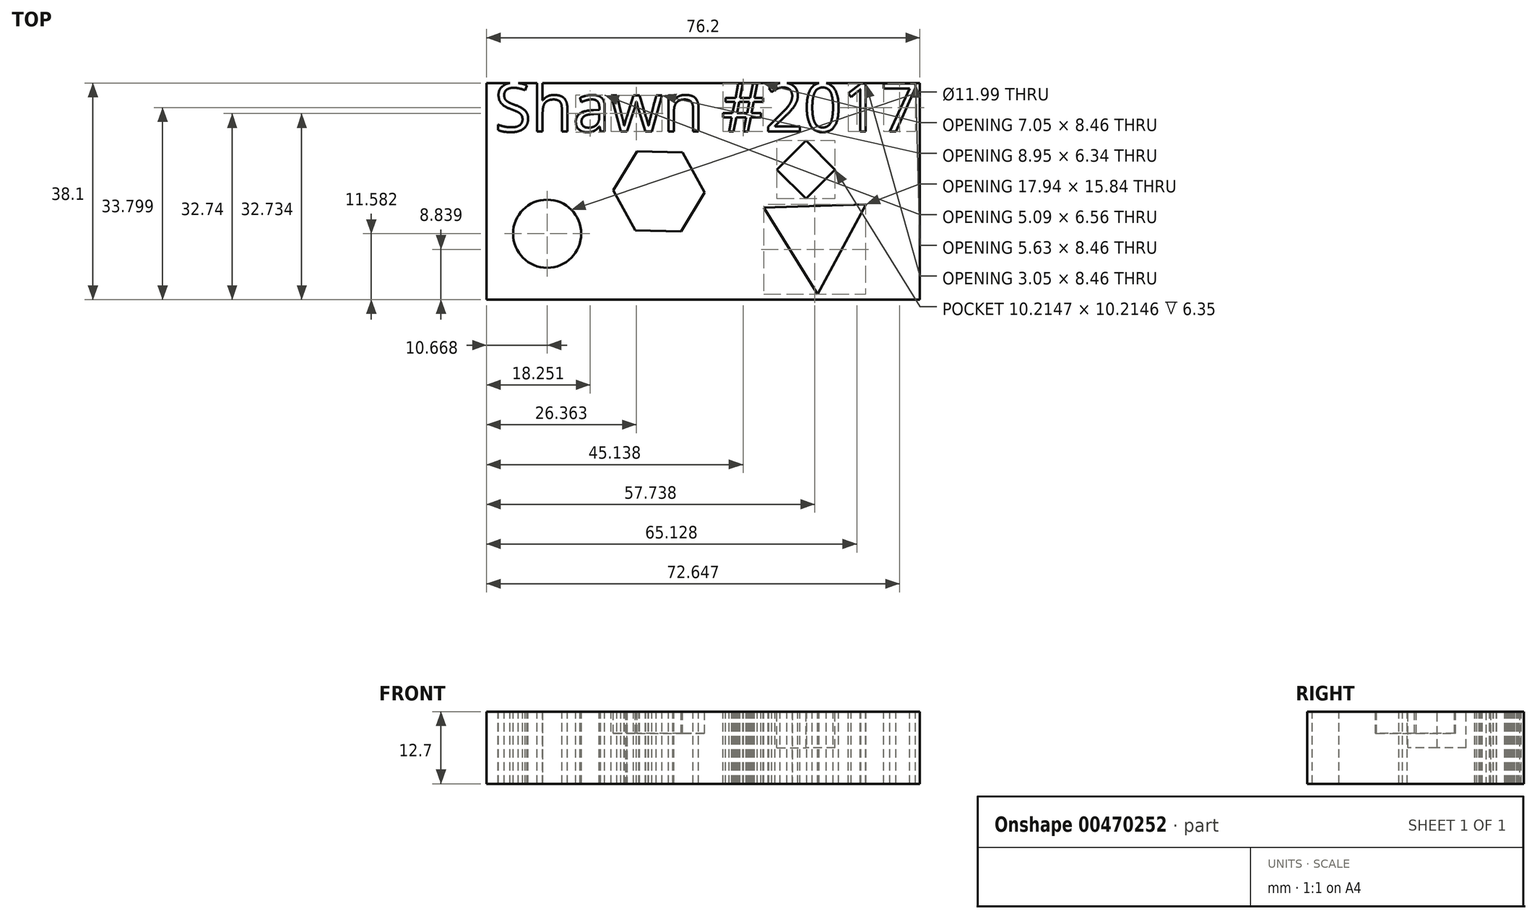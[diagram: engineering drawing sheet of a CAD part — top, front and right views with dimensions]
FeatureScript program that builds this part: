
annotation { "Feature Type Name" : "Feature", "Feature Type Description" : "" }
export const myFeature = defineFeature(function(context is Context, id is Id, definition is map)
    precondition{}
    {
        {
            var Q0;
            Q0=qCreatedBy(makeId("Top.planeOp"),FACE);
            var sketch = newSketch(context, id + "F0", { "sketchPlane" : qUnion([Q0])});
            skLineSegment(sketch, "E0.bottom", {"start": v(38.1, -19.05) * mm, "end": v(-38.1, -19.05) * mm});
            skLineSegment(sketch, "E0.top", {"start": v(38.1, 19.05) * mm, "end": v(-38.1, 19.05) * mm});
            skLineSegment(sketch, "E0.left", {"start": v(38.1, -19.05) * mm, "end": v(38.1, 19.05) * mm});
            skLineSegment(sketch, "E0.right", {"start": v(-38.1, -19.05) * mm, "end": v(-38.1, 19.05) * mm});
            skPoint(sketch, "E0.middle", {"position": v(0, 0) * mm});
            skSolve(sketch);
        }
        {
            var Q0;
            Q0 = qSketchRegion(id + "F0", true);
            extrude(context, id + "F1", {"entities" : qUnion([Q0]), "depth" : 12.7 * mm});
        }
        {
            var Q0;
            Q0=makeQuery(id+"F1.opExtrude","CAP_FACE",FACE,{"disambiguationData":[OSD([sQuery(id+"F0.wireOp",EDGE,"E0.bottom"),sQuery(id+"F0.wireOp",EDGE,"E0.top"),sQuery(id+"F0.wireOp",EDGE,"E0.left"),sQuery(id+"F0.wireOp",EDGE,"E0.right")])],"isStart":false});
            var sketch = newSketch(context, id + "F2", { "sketchPlane" : qUnion([Q0])});
            skCircle(sketch, "E1.cCircle", {"center": v(-7.77, 0) * mm, "radius": 6.96 * mm, "construction": true});
            skLineSegment(sketch, "E1.0", {"start": v(-11.93, -6.87) * mm, "end": v(-15.8, 0.17) * mm});
            skLineSegment(sketch, "E1.1", {"start": v(-15.8, 0.17) * mm, "end": v(-11.64, 7.04) * mm});
            skLineSegment(sketch, "E1.2", {"start": v(-11.64, 7.04) * mm, "end": v(-3.61, 6.87) * mm});
            skLineSegment(sketch, "E1.3", {"start": v(-3.61, 6.87) * mm, "end": v(0.26, -0.17) * mm});
            skLineSegment(sketch, "E1.4", {"start": v(0.26, -0.17) * mm, "end": v(-3.9, -7.04) * mm});
            skLineSegment(sketch, "E1.5", {"start": v(-3.9, -7.04) * mm, "end": v(-11.93, -6.87) * mm});
            skPoint(sketch, "E1.0.midPoint", {"position": v(-13.87, -3.35) * mm});
            skSolve(sketch);
        }
        {
            var Q0;
            Q0=makeQuery(id+"F2.imprint","IMPRINT",FACE,{"disambiguationData":[TD([[makeQuery(id+"F2.imprint","IMPRINT",EDGE,{"derivedFrom":sQuery(id+"F2.wireOp",EDGE,"E1.0")}),-1.0]])]});
            extrude(context, id + "F3", {"entities" : qUnion([Q0]), "operationType" : NewBodyOperationType.REMOVE, "oppositeDirection" : true, "depth" : 3.8 * mm});
        }
        {
            var Q0;
            Q0=makeQuery(id+"F1.opExtrude","CAP_FACE",FACE,{"disambiguationData":[OSD([sQuery(id+"F0.wireOp",EDGE,"E0.bottom"),sQuery(id+"F0.wireOp",EDGE,"E0.top"),sQuery(id+"F0.wireOp",EDGE,"E0.left"),sQuery(id+"F0.wireOp",EDGE,"E0.right")])],"isStart":false});
            var sketch = newSketch(context, id + "F4", { "sketchPlane" : qUnion([Q0])});
            skCircle(sketch, "E2", {"center": v(-27.43, -7.47) * mm, "radius": 6 * mm});
            skSolve(sketch);
        }
        {
            var Q0;
            Q0=makeQuery(id+"F4.imprint","IMPRINT",FACE,{"disambiguationData":[TD([[makeQuery(id+"F4.imprint","IMPRINT",EDGE,{"derivedFrom":sQuery(id+"F4.wireOp",EDGE,"E2")}),1.0]])]});
            extrude(context, id + "F5", {"entities" : qUnion([Q0]), "operationType" : NewBodyOperationType.REMOVE, "oppositeDirection" : true, "depth" : 12.7 * mm});
        }
        {
            var Q0;
            Q0=makeQuery(id+"F1.opExtrude","CAP_FACE",FACE,{"disambiguationData":[OSD([sQuery(id+"F0.wireOp",EDGE,"E0.bottom"),sQuery(id+"F0.wireOp",EDGE,"E0.top"),sQuery(id+"F0.wireOp",EDGE,"E0.left"),sQuery(id+"F0.wireOp",EDGE,"E0.right")])],"isStart":false});
            var sketch = newSketch(context, id + "F6", { "sketchPlane" : qUnion([Q0])});
            skCircle(sketch, "E3.cCircle", {"center": v(19.81, -7.77) * mm, "radius": 5.18 * mm, "construction": true});
            skLineSegment(sketch, "E3.0", {"start": v(28.6, -2.3) * mm, "end": v(20.16, -18.13) * mm});
            skLineSegment(sketch, "E3.1", {"start": v(20.16, -18.13) * mm, "end": v(10.67, -2.9) * mm});
            skLineSegment(sketch, "E3.2", {"start": v(10.67, -2.9) * mm, "end": v(28.6, -2.3) * mm});
            skPoint(sketch, "E3.0.midPoint", {"position": v(24.38, -10.21) * mm});
            skSolve(sketch);
        }
        {
            var Q0;
            Q0=makeQuery(id+"F6.imprint","IMPRINT",FACE,{"disambiguationData":[TD([[makeQuery(id+"F6.imprint","IMPRINT",EDGE,{"derivedFrom":sQuery(id+"F6.wireOp",EDGE,"E3.0")}),-1.0]])]});
            extrude(context, id + "F7", {"entities" : qUnion([Q0]), "operationType" : NewBodyOperationType.REMOVE, "oppositeDirection" : true, "depth" : 12.7 * mm});
        }
        {
            var Q0;
            Q0=makeQuery(id+"F1.opExtrude","CAP_FACE",FACE,{"disambiguationData":[OSD([sQuery(id+"F0.wireOp",EDGE,"E0.bottom"),sQuery(id+"F0.wireOp",EDGE,"E0.top"),sQuery(id+"F0.wireOp",EDGE,"E0.left"),sQuery(id+"F0.wireOp",EDGE,"E0.right")])],"isStart":false});
            var sketch = newSketch(context, id + "F8", { "sketchPlane" : qUnion([Q0])});
            skText(sketch, "E4", { "text": "Shawn #2017", "fontName": "OpenSans-Regular.ttf"});
            const initialGuessF8  = {"E4": [-0.03671, 0.01052, 1, 0, 0.00853]};
            skSetInitialGuess(sketch, initialGuessF8);
            skSolve(sketch);
        }
        {
            var Q0;
            Q0 = qSketchRegion(id + "F8", true);
            extrude(context, id + "F9", {"entities" : qUnion([Q0]), "operationType" : NewBodyOperationType.REMOVE, "oppositeDirection" : true, "depth" : 12.7 * mm});
        }
        {
            var Q0;
            {var subQ0=sQuery(id+"F0.wireOp",EDGE,"E0.top");var subQ1=sQuery(id+"F0.wireOp",EDGE,"E0.bottom");var subQ2=sQuery(id+"F0.wireOp",EDGE,"E0.left");var subQ3=sQuery(id+"F0.wireOp",EDGE,"E0.right");Q0=makeQuery(id+"F9.boolean.opBoolean","SPLIT",FACE,{"disambiguationData":[TD([makeQuery(id+"F1.opExtrude","SWEPT_FACE",FACE,{"disambiguationData":[OSD([subQ1])]})])],"derivedFrom":makeQuery(id+"F1.opExtrude","CAP_FACE",FACE,{"disambiguationData":[OSD([subQ1,subQ0,subQ2,subQ3])],"isStart":false})});}
            var sketch = newSketch(context, id + "F10", { "sketchPlane" : qUnion([Q0])});
            skCircle(sketch, "E5.cCircle", {"center": v(18.1, 3.82) * mm, "radius": 5.1 * mm, "construction": true});
            skLineSegment(sketch, "E5.0", {"start": v(23.2, 3.82) * mm, "end": v(18.1, -1.28) * mm});
            skLineSegment(sketch, "E5.1", {"start": v(18.1, -1.28) * mm, "end": v(12.99, 3.82) * mm});
            skLineSegment(sketch, "E5.2", {"start": v(12.99, 3.82) * mm, "end": v(18.1, 8.93) * mm});
            skLineSegment(sketch, "E5.3", {"start": v(18.1, 8.93) * mm, "end": v(23.2, 3.82) * mm});
            skSolve(sketch);
        }
        {
            var Q0;
            Q0=makeQuery(id+"F10.imprint","IMPRINT",FACE,{"disambiguationData":[TD([[makeQuery(id+"F10.imprint","IMPRINT",EDGE,{"derivedFrom":sQuery(id+"F10.wireOp",EDGE,"E5.0")}),-1.0]])]});
            extrude(context, id + "F11", {"entities" : qUnion([Q0]), "operationType" : NewBodyOperationType.REMOVE, "oppositeDirection" : true, "depth" : 6.35 * mm});
        }
    });
